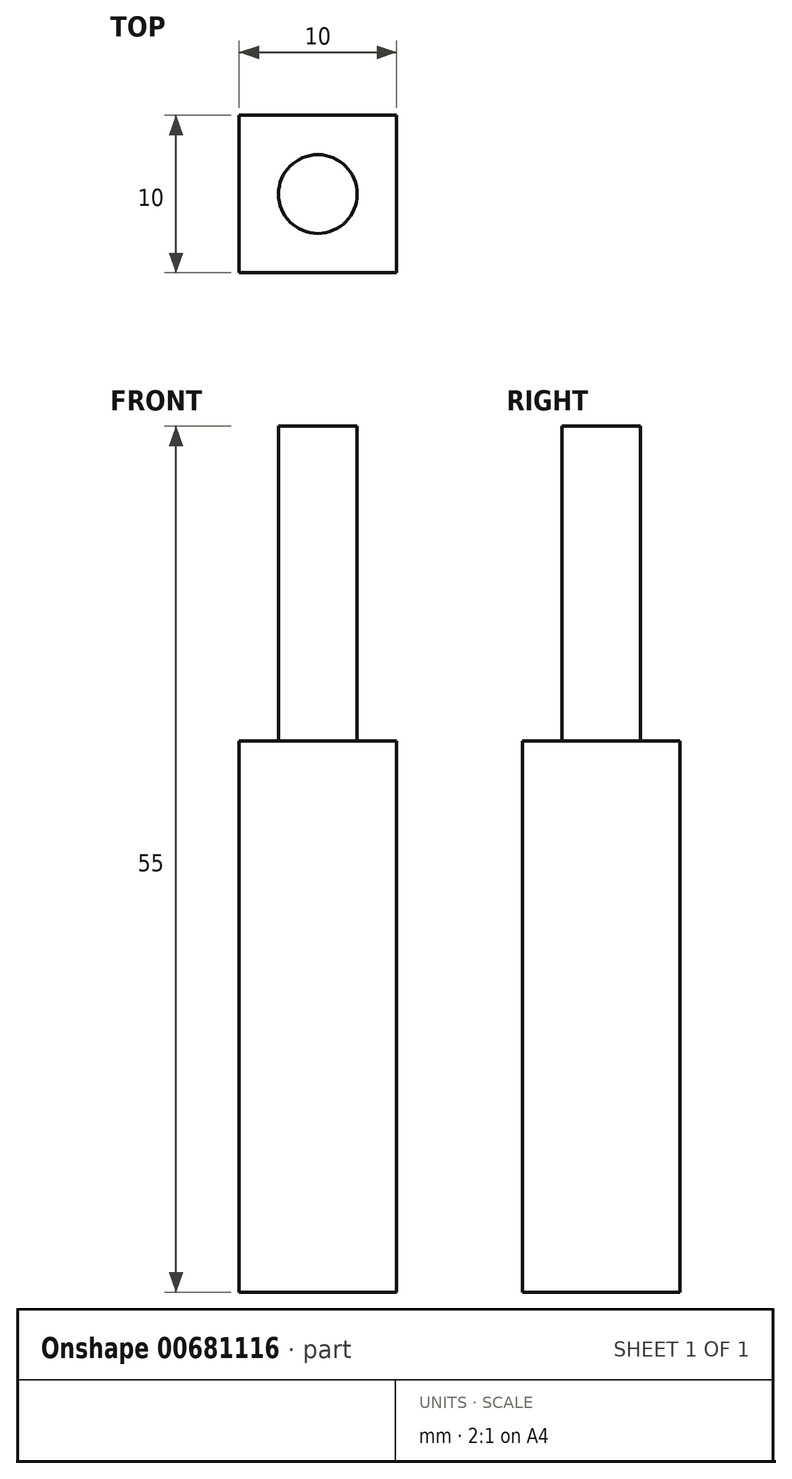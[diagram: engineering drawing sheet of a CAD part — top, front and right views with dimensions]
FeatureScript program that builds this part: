
annotation { "Feature Type Name" : "Feature", "Feature Type Description" : "" }
export const myFeature = defineFeature(function(context is Context, id is Id, definition is map)
    precondition{}
    {
        {
            var Q0;
            Q0=qCreatedBy(makeId("Top.planeOp"),FACE);
            var sketch = newSketch(context, id + "F0", { "sketchPlane" : qUnion([Q0])});
            skLineSegment(sketch, "E0.bottom", {"start": v(-5, 5) * mm, "end": v(5, 5) * mm});
            skLineSegment(sketch, "E0.top", {"start": v(-5, -5) * mm, "end": v(5, -5) * mm});
            skLineSegment(sketch, "E0.left", {"start": v(-5, 5) * mm, "end": v(-5, -5) * mm});
            skLineSegment(sketch, "E0.right", {"start": v(5, 5) * mm, "end": v(5, -5) * mm});
            skPoint(sketch, "E0.middle", {"position": v(0, 0) * mm});
            skSolve(sketch);
        }
        {
            var Q0;
            Q0=makeQuery(id+"F0.imprint","IMPRINT",FACE,{"disambiguationData":[TD([[makeQuery(id+"F0.imprint","IMPRINT",EDGE,{"derivedFrom":sQuery(id+"F0.wireOp",EDGE,"E0.bottom")}),-1.0]])]});
            extrude(context, id + "F1", {"entities" : qUnion([Q0]), "depth" : 35 * mm, "offsetDistance" : 25 * mm});
        }
        {
            var Q0;
            Q0=makeQuery(id+"F1.opExtrude","CAP_FACE",FACE,{"disambiguationData":[OSD([sQuery(id+"F0.wireOp",EDGE,"E0.bottom"),sQuery(id+"F0.wireOp",EDGE,"E0.top"),sQuery(id+"F0.wireOp",EDGE,"E0.left"),sQuery(id+"F0.wireOp",EDGE,"E0.right")])],"isStart":false});
            var sketch = newSketch(context, id + "F2", { "sketchPlane" : qUnion([Q0])});
            skCircle(sketch, "E1", {"center": v(0, 0) * mm, "radius": 2.5 * mm});
            skSolve(sketch);
        }
        {
            var Q0;
            Q0=makeQuery(id+"F2.imprint","IMPRINT",FACE,{"disambiguationData":[TD([[makeQuery(id+"F2.imprint","IMPRINT",EDGE,{"derivedFrom":sQuery(id+"F2.wireOp",EDGE,"E1")}),1.0]])]});
            var Q1;
            Q1=sQuery(id+"F2.wireOp",EDGE,"E1");
            extrude(context, id + "F3", {"entities" : qUnion([Q0]), "operationType" : NewBodyOperationType.ADD, "surfaceEntities" : qUnion([Q1]), "depth" : 20 * mm, "offsetDistance" : 25 * mm});
        }
    });
